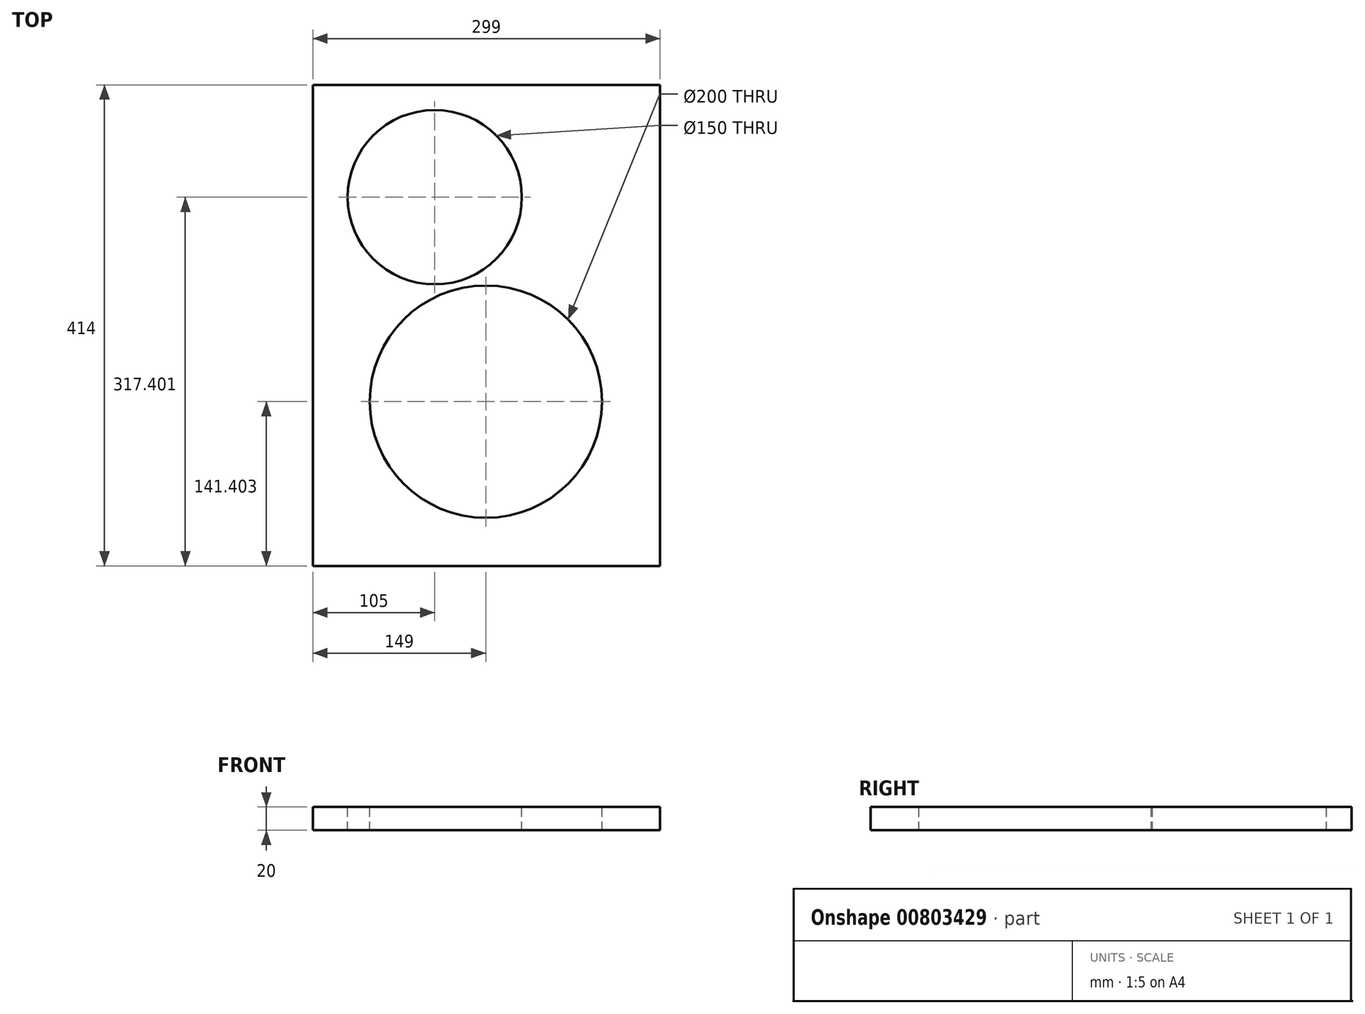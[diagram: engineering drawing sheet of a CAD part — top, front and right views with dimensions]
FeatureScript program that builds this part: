
annotation { "Feature Type Name" : "Feature", "Feature Type Description" : "" }
export const myFeature = defineFeature(function(context is Context, id is Id, definition is map)
    precondition{}
    {
        {
            var Q0;
            Q0=qCreatedBy(makeId("Top.planeOp"),FACE);
            var sketch = newSketch(context, id + "F0", { "sketchPlane" : qUnion([Q0])});
            skLineSegment(sketch, "E0.bottom", {"start": v(0, 0) * mm, "end": v(299, 0) * mm});
            skLineSegment(sketch, "E0.top", {"start": v(0, 414) * mm, "end": v(299, 414) * mm});
            skLineSegment(sketch, "E0.left", {"start": v(0, 0) * mm, "end": v(0, 414) * mm});
            skLineSegment(sketch, "E0.right", {"start": v(299, 0) * mm, "end": v(299, 414) * mm});
            skSolve(sketch);
        }
        {
            var Q0;
            Q0 = qSketchRegion(id + "F0", true);
            extrude(context, id + "F1", {"entities" : qUnion([Q0]), "depth" : 20 * mm, "offsetDistance" : 25 * mm});
        }
        {
            var Q0;
            Q0=makeQuery(id+"F1.opExtrude","CAP_FACE",FACE,{"disambiguationData":[OSD([sQuery(id+"F0.wireOp",EDGE,"E0.bottom"),sQuery(id+"F0.wireOp",EDGE,"E0.top"),sQuery(id+"F0.wireOp",EDGE,"E0.left"),sQuery(id+"F0.wireOp",EDGE,"E0.right")])],"isStart":false});
            var sketch = newSketch(context, id + "F2", { "sketchPlane" : qUnion([Q0])});
            skEllipse(sketch, "E1", {"center": v(149, 141.4) * mm, "majorRadius": 100 * mm, "minorRadius": 100 * mm, "majorAxis": v(0, -1)});
            skCircle(sketch, "E2", {"center": v(105, 317.4) * mm, "radius": 75 * mm});
            skSolve(sketch);
        }
        {
            var Q0;
            Q0=makeQuery(id+"F2.imprint","IMPRINT",FACE,{"disambiguationData":[TD([[makeQuery(id+"F2.imprint","IMPRINT",EDGE,{"derivedFrom":sQuery(id+"F2.wireOp",EDGE,"E2")}),1.0]])]});
            var Q1;
            Q1=makeQuery(id+"F2.imprint","IMPRINT",FACE,{"disambiguationData":[TD([[makeQuery(id+"F2.imprint","IMPRINT",EDGE,{"derivedFrom":sQuery(id+"F2.wireOp",EDGE,"E1")}),1.0]])]});
            extrude(context, id + "F3", {"entities" : qUnion([Q0, Q1]), "operationType" : NewBodyOperationType.REMOVE, "endBound" : BoundingType.THROUGH_ALL, "oppositeDirection" : true, "depth" : 25 * mm, "offsetDistance" : 25 * mm});
        }
    });
